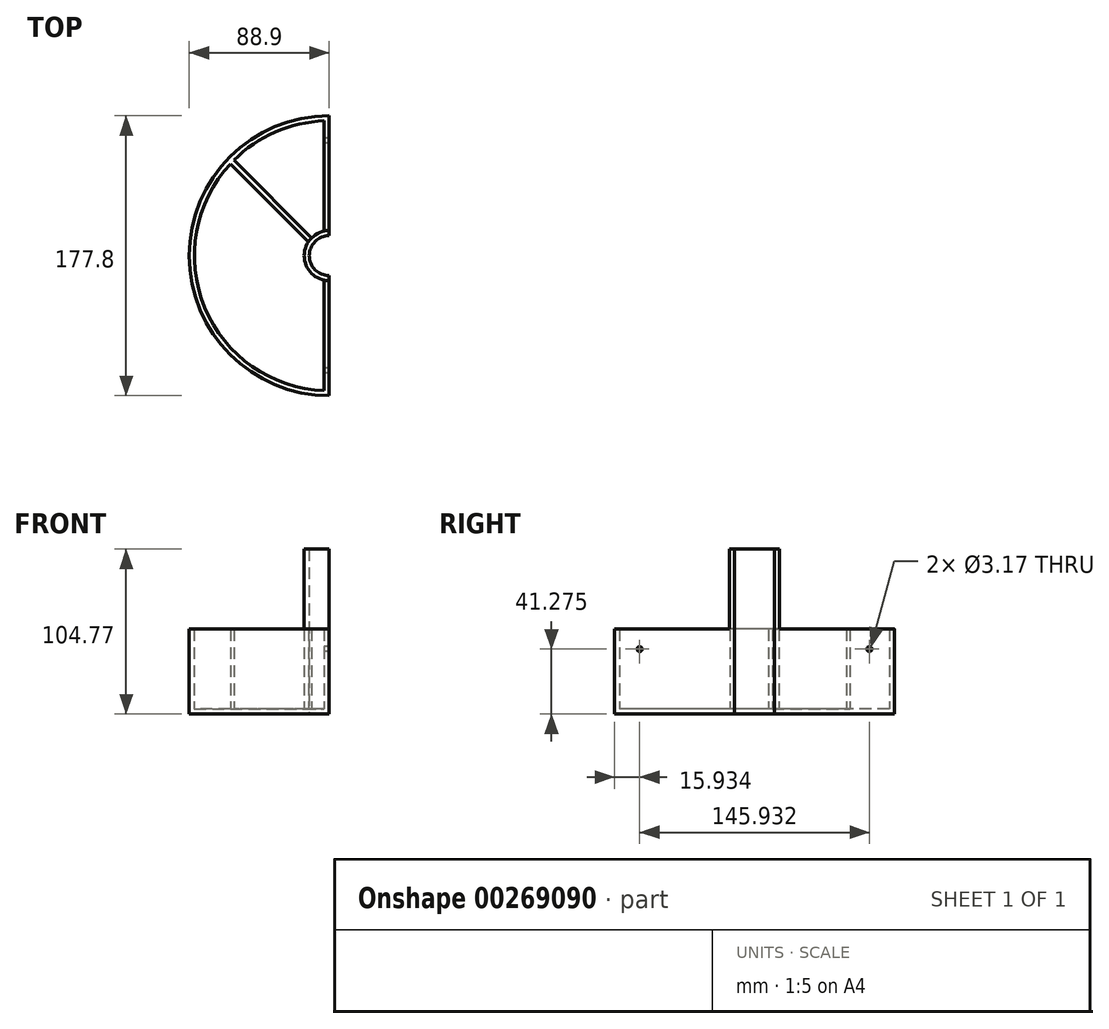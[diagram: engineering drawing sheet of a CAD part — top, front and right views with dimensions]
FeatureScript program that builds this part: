
annotation { "Feature Type Name" : "Feature", "Feature Type Description" : "" }
export const myFeature = defineFeature(function(context is Context, id is Id, definition is map)
    precondition{}
    {
        {
            var Q0;
            Q0=qCreatedBy(makeId("Top.planeOp"),FACE);
            var sketch = newSketch(context, id + "F0", { "sketchPlane" : qUnion([Q0])});
            skArc(sketch, "E0", {"start": v(0, 88.9) * mm, "mid": v(-88.9, 0) * mm, "end": v(0, -88.9) * mm});
            skArc(sketch, "E1", {"start": v(0, 12.7) * mm, "mid": v(-12.7, 0) * mm, "end": v(0, -12.7) * mm});
            skLineSegment(sketch, "E2", {"start": v(0, 88.9) * mm, "end": v(0, 12.7) * mm});
            skLineSegment(sketch, "E3.trimOffspring", {"start": v(0, -12.7) * mm, "end": v(0, -88.9) * mm});
            skSolve(sketch);
        }
        {
            var Q0;
            Q0=makeQuery(id+"F0.imprint","IMPRINT",FACE,{"disambiguationData":[TD([[makeQuery(id+"F0.imprint","IMPRINT",EDGE,{"derivedFrom":sQuery(id+"F0.wireOp",EDGE,"E0")}),1.0]])]});
            extrude(context, id + "F1", {"entities" : qUnion([Q0]), "depth" : 3.17 * mm});
        }
        {
            var Q0;
            Q0=makeQuery(id+"F1.opExtrude","CAP_FACE",FACE,{"disambiguationData":[OSD([sQuery(id+"F0.wireOp",EDGE,"E0"),sQuery(id+"F0.wireOp",EDGE,"E1"),sQuery(id+"F0.wireOp",EDGE,"E2"),sQuery(id+"F0.wireOp",EDGE,"E3.trimOffspring")])],"isStart":false});
            var sketch = newSketch(context, id + "F2", { "sketchPlane" : qUnion([Q0])});
            skArc(sketch, "E4", {"start": v(0, 12.7) * mm, "mid": v(-12.7, 0) * mm, "end": v(0, -12.7) * mm});
            skArc(sketch, "E5", {"start": v(0, 88.9) * mm, "mid": v(-62.86, 62.86) * mm, "end": v(-88.9, 0) * mm});
            skLineSegment(sketch, "E6", {"start": v(0, 88.9) * mm, "end": v(0, 12.7) * mm});
            skLineSegment(sketch, "E7.trimOffspring", {"start": v(0, -12.7) * mm, "end": v(0, -88.9) * mm});
            skArc(sketch, "E8", {"start": v(-3.18, 15.55) * mm, "mid": v(-7.52, 13.98) * mm, "end": v(-11.23, 11.23) * mm});
            skArc(sketch, "E9", {"start": v(-3.18, 85.67) * mm, "mid": v(-34.27, 78.58) * mm, "end": v(-60.62, 60.62) * mm});
            skLineSegment(sketch, "E10", {"start": v(-3.18, 85.67) * mm, "end": v(-3.18, 15.55) * mm});
            skLineSegment(sketch, "E11.trimOffspring", {"start": v(-3.17, -15.55) * mm, "end": v(-3.17, -85.67) * mm});
            skArc(sketch, "E12", {"start": v(-88.9, 0) * mm, "mid": v(-62.86, -62.86) * mm, "end": v(0, -88.9) * mm});
            skLineSegment(sketch, "E13", {"start": v(-62.82, 58.33) * mm, "end": v(-13.24, 8.75) * mm});
            skLineSegment(sketch, "E14", {"start": v(-11.23, 11.23) * mm, "end": v(-60.62, 60.62) * mm});
            skPoint(sketch, "E15.end.orphan", {"position": v(-62.86, 62.86) * mm});
            skArc(sketch, "E16.trimOffspring", {"start": v(-62.82, 58.33) * mm, "mid": v(-79.2, -32.8) * mm, "end": v(-3.17, -85.67) * mm});
            skArc(sketch, "E17.trimOffspring", {"start": v(-13.24, 8.75) * mm, "mid": v(-14.67, -6.08) * mm, "end": v(-3.17, -15.55) * mm});
            skSolve(sketch);
        }
        {
            var Q0;
            Q0=makeQuery(id+"F2.imprint","IMPRINT",FACE,{"disambiguationData":[TD([[makeQuery(id+"F2.imprint","IMPRINT",EDGE,{"derivedFrom":sQuery(id+"F2.wireOp",EDGE,"E4")}),-1.0]])]});
            extrude(context, id + "F3", {"entities" : qUnion([Q0]), "operationType" : NewBodyOperationType.ADD, "depth" : 50.8 * mm});
        }
        {
            var Q0;
            Q0=makeQuery(id+"F3.opExtrude","CAP_FACE",FACE,{"disambiguationData":[OSD([sQuery(id+"F2.wireOp",EDGE,"E4"),sQuery(id+"F2.wireOp",EDGE,"E5"),sQuery(id+"F2.wireOp",EDGE,"E6"),sQuery(id+"F2.wireOp",EDGE,"E7.trimOffspring"),sQuery(id+"F2.wireOp",EDGE,"E8"),sQuery(id+"F2.wireOp",EDGE,"E9"),sQuery(id+"F2.wireOp",EDGE,"E10"),sQuery(id+"F2.wireOp",EDGE,"E11.trimOffspring"),sQuery(id+"F2.wireOp",EDGE,"E12"),sQuery(id+"F2.wireOp",EDGE,"E13"),sQuery(id+"F2.wireOp",EDGE,"E14"),sQuery(id+"F2.wireOp",EDGE,"E16.trimOffspring"),sQuery(id+"F2.wireOp",EDGE,"E17.trimOffspring")])],"isStart":false});
            var sketch = newSketch(context, id + "F4", { "sketchPlane" : qUnion([Q0])});
            skArc(sketch, "E18", {"start": v(0, 12.7) * mm, "mid": v(-12.7, 0) * mm, "end": v(0, -12.7) * mm});
            skArc(sketch, "E19", {"start": v(0, 15.88) * mm, "mid": v(-15.88, 0) * mm, "end": v(0, -15.88) * mm});
            skLineSegment(sketch, "E20", {"start": v(0, 15.88) * mm, "end": v(0, 12.7) * mm});
            skLineSegment(sketch, "E21.trimOffspring", {"start": v(0, -12.7) * mm, "end": v(0, -15.88) * mm});
            skSolve(sketch);
        }
        {
            var Q0;
            Q0=makeQuery(id+"F4.imprint","IMPRINT",FACE,{"disambiguationData":[TD([[makeQuery(id+"F4.imprint","IMPRINT",EDGE,{"derivedFrom":sQuery(id+"F4.wireOp",EDGE,"E18")}),-1.0]])]});
            extrude(context, id + "F5", {"entities" : qUnion([Q0]), "operationType" : NewBodyOperationType.ADD, "depth" : 50.8 * mm});
        }
        {
            var Q0;
            Q0=makeQuery(id+"F3.opExtrude","SWEPT_FACE",FACE,{"disambiguationData":[OSD([sQuery(id+"F2.wireOp",EDGE,"E11.trimOffspring")])]});
            var sketch = newSketch(context, id + "F6", { "sketchPlane" : qUnion([Q0])});
            skCircle(sketch, "E22", {"center": v(72.97, 41.27) * mm, "radius": 1.59 * mm});
            skCircle(sketch, "E23", {"center": v(-72.97, 41.27) * mm, "radius": 1.59 * mm});
            skSolve(sketch);
        }
        {
            var Q0;
            Q0 = qSketchRegion(id + "F6", true);
            extrude(context, id + "F7", {"entities" : qUnion([Q0]), "operationType" : NewBodyOperationType.REMOVE, "oppositeDirection" : true, "depth" : 3.17 * mm});
        }
    });
